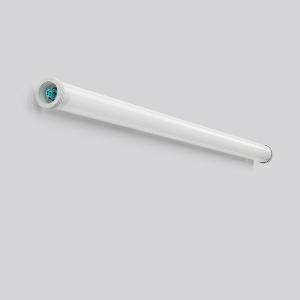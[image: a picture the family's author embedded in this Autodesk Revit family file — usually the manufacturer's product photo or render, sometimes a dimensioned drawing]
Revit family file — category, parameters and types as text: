
# Revit family: planox_tube_601072_002_76_deaf
name_source: partatom
category: Lighting Fixtures
units: mm (PartAtom-declared; Revit-internal decimal feet)

## family parameters
Cut with Voids When Loaded = No
Host = Face
Light Source = No
Part Type = Normal
Room Calculation Point = No
Round Connector Dimension = Use Diameter
Shared = No

## types (1)
- PLANOX TUBE (1 x LED Modul 840, 8650 lm, 4000)
    Apparent Load = 62 VA
    CIE Flux Codes = 42 71 90 91 100
    Color Rendering = 80
    Color Temperature = 4000
    Default Elevation = 1800 mm
    Description = Series: PLANOX TUBE
Robust protective tube luminaire for tough requirements. Rack made of sheet steel, white powder coated. End caps made of plastic (polyamide) grey. Diffuser made of plastic (polycarbonate), opal, shockproof. Symmetrical light distribution. Homogeneous light distribution. With accessories for wall, ceiling or pendant mounting. Driver integrated.Easy installation with the Plug+Play Wieland RST CLASSIC plug-in system. Mounting set must be ordered separately. Luminaire with limited surface temperature in accordance with EN 60598-2-24 for use in environments in which a deposit of conductive dust on the luminaire can be expected. Qualified for use in the food and drink industry. Suitable for lighting in public car parks and public off-street parking spaces according to DIN 67528. Environmentally friendly and resource-saving due to replaceable components. 
Colour: white
Diameter: 78 mm
Length: 1564 mm
Lamp: LED
Socket: without socket
Colour temperature: 4000K
Colour rendering index (CRI): 83
System power: 62 W
Rated luminous flux: 8650 lm
Luminous efficiency: 140 lm/W
Control gear: Converter, dimmable, DALI
Protection class: I
Type of protection: IP 67
    Height = 0 mm  [stored 0 ft]
    Lamp = 1 x LED Modul 840
    Lamp Light Flux = 8650 lm
    Lamp count = 1
    Length = 1564 mm
    Lifetime = 50000 h
    Luminous efficacy = 140 lm/W
    Manufacturer = RZB
    ModVariant = No
    Model = 601072.002.76
    Mounting Place = Ceiling
    Mounting Type = Surface mounted
    Number of Poles = 1
    OnlyDefault = Yes
    Power Factor = 1
    Product Name = PLANOX TUBE
    Product group = Surface mounted luminaires for moist/humid enviroments
    ProductGroupID = 308
    Protection Class = Protection class I
    Protection Degree = Degree of protection
    RLX_Detail_Level = 1
    RLX_Emergency_Light_Flux = 0 lm
    RLX_Emergency_Type = 0
    RLX_Emergency_Type_DB = No
    RlxData = <blob elided: 34909 chars, md5=faf73a2e>
    Socket = socket
    Standby Power = 0 W
    System Light Flux = 8650 lm
    System Power = 62 W
    Type Comments = Product without accessories
    Type Image = 601072.002.76.jpg
    URL = http://relux.com
    VarID = ---
    Voltage = 0 V
    Weight = 0.00 kg
    Width = 0 mm  [stored 0 ft]

note: [stored X ft] marks values corroborated as IEEE doubles in the binary element streams (Revit-internal decimal feet)

## geometry (parser evidence)
native form markers: Blend x4, Sweep x12
no freeform markers — native parametric forms only
